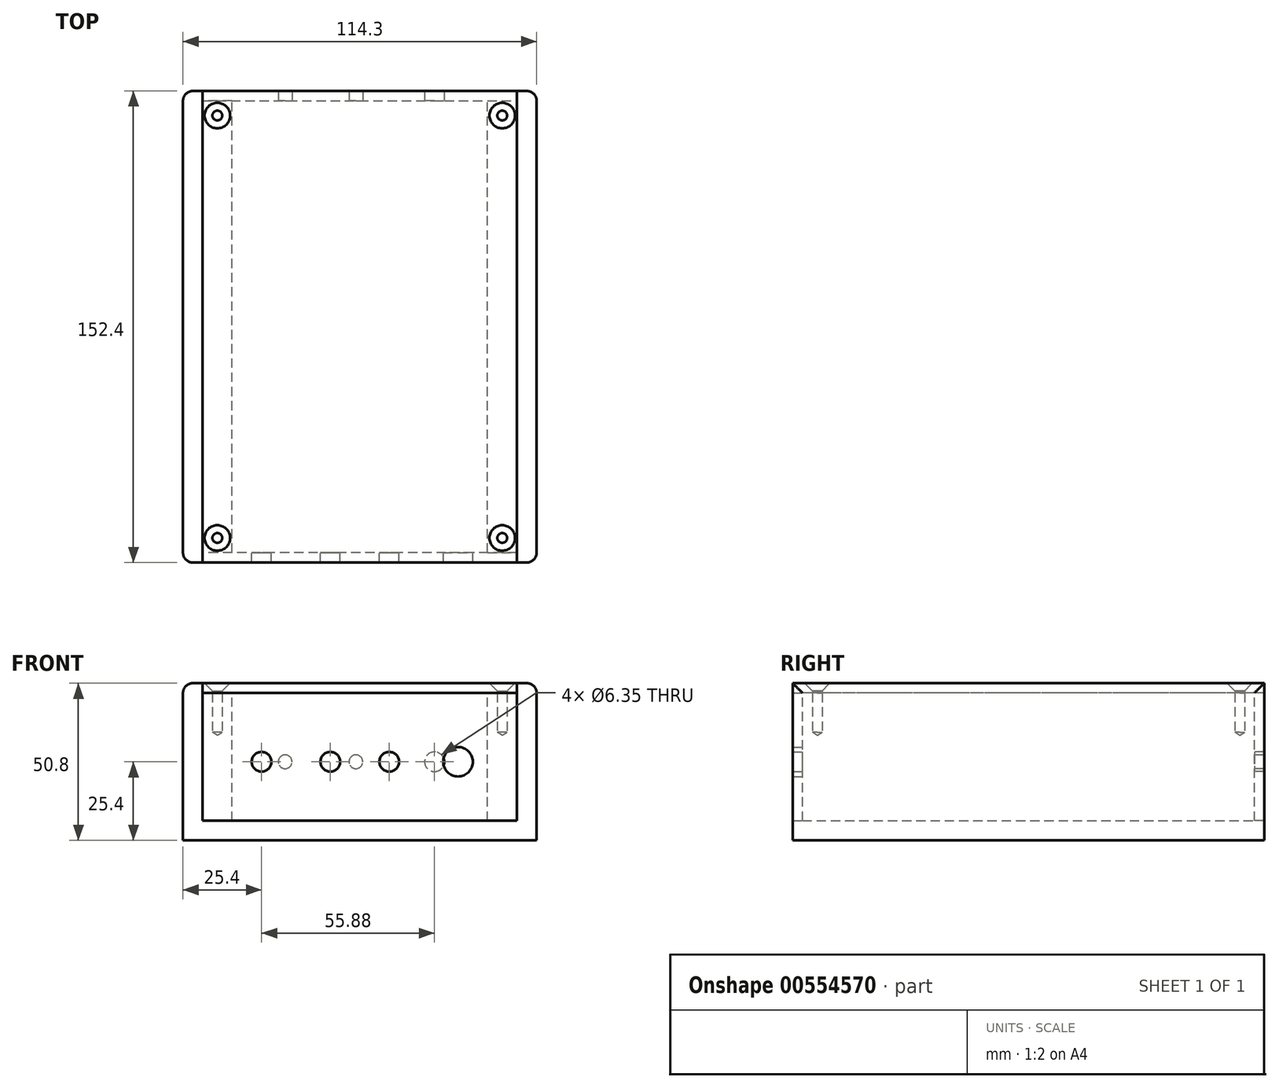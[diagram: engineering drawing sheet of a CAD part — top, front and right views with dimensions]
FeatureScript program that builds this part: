
annotation { "Feature Type Name" : "Feature", "Feature Type Description" : "" }
export const myFeature = defineFeature(function(context is Context, id is Id, definition is map)
    precondition{}
    {
        {
            var Q0;
            Q0=qCreatedBy(makeId("Top.planeOp"),FACE);
            var sketch = newSketch(context, id + "F0", { "sketchPlane" : qUnion([Q0])});
            skLineSegment(sketch, "E0.bottom", {"start": v(57.15, 76.2) * mm, "end": v(-57.15, 76.2) * mm});
            skLineSegment(sketch, "E0.top", {"start": v(57.15, -76.2) * mm, "end": v(-57.15, -76.2) * mm});
            skLineSegment(sketch, "E0.left", {"start": v(57.15, 76.2) * mm, "end": v(57.15, -76.2) * mm});
            skLineSegment(sketch, "E0.right", {"start": v(-57.15, 76.2) * mm, "end": v(-57.15, -76.2) * mm});
            skPoint(sketch, "E0.middle", {"position": v(0, 0) * mm});
            skLineSegment(sketch, "E1", {"start": v(0, -76.2) * mm, "end": v(0, 76.2) * mm, "construction": true});
            skLineSegment(sketch, "E2", {"start": v(-57.15, 0) * mm, "end": v(57.15, 0) * mm, "construction": true});
            skSolve(sketch);
        }
        {
            var Q0;
            Q0=makeQuery(id+"F0.imprint","IMPRINT",FACE,{"disambiguationData":[TD([[makeQuery(id+"F0.imprint","IMPRINT",EDGE,{"derivedFrom":sQuery(id+"F0.wireOp",EDGE,"E0.bottom")}),1.0]])]});
            extrude(context, id + "F1", {"entities" : qUnion([Q0]), "depth" : 50.8 * mm, "offsetDistance" : 25.4 * mm});
        }
        {
            var Q0;
            Q0=makeQuery(id+"F1.opExtrude","CAP_FACE",FACE,{"disambiguationData":[OSD([sQuery(id+"F0.wireOp",EDGE,"E0.bottom"),sQuery(id+"F0.wireOp",EDGE,"E0.top"),sQuery(id+"F0.wireOp",EDGE,"E0.left"),sQuery(id+"F0.wireOp",EDGE,"E0.right")])],"isStart":false});
            var sketch = newSketch(context, id + "F2", { "sketchPlane" : qUnion([Q0])});
            skLineSegment(sketch, "E3.bottom", {"start": v(50.8, 76.2) * mm, "end": v(-50.8, 76.2) * mm});
            skLineSegment(sketch, "E3.top", {"start": v(50.8, -76.2) * mm, "end": v(-50.8, -76.2) * mm});
            skLineSegment(sketch, "E3.left", {"start": v(50.8, 76.2) * mm, "end": v(50.8, -76.2) * mm});
            skLineSegment(sketch, "E3.right", {"start": v(-50.8, 76.2) * mm, "end": v(-50.8, -76.2) * mm});
            skPoint(sketch, "E3.middle", {"position": v(0, 0) * mm});
            skSolve(sketch);
        }
        {
            var Q0;
            Q0 = qSketchRegion(id + "F2", true);
            extrude(context, id + "F3", {"entities" : qUnion([Q0]), "operationType" : NewBodyOperationType.REMOVE, "endBound" : BoundingType.UP_TO_NEXT, "oppositeDirection" : true, "depth" : 25.4 * mm, "hasOffset" : true, "offsetDistance" : 6.35 * mm});
        }
        {
            var Q0;
            Q0=makeQuery(id+"F3.boolean.opBoolean","COPY",FACE,{"derivedFrom":makeQuery(id+"F3.opExtrude","SWEPT_FACE",FACE,{"disambiguationData":[OSD([sQuery(id+"F2.wireOp",EDGE,"E3.left")])]})});
            var sketch = newSketch(context, id + "F4", { "sketchPlane" : qUnion([Q0])});
            skLineSegment(sketch, "E4.bottom", {"start": v(-73.02, 6.35) * mm, "end": v(73.02, 6.35) * mm});
            skLineSegment(sketch, "E4.top", {"start": v(-73.02, 47.63) * mm, "end": v(73.02, 47.63) * mm});
            skLineSegment(sketch, "E4.left", {"start": v(-73.02, 6.35) * mm, "end": v(-73.02, 47.63) * mm});
            skLineSegment(sketch, "E4.right", {"start": v(73.02, 6.35) * mm, "end": v(73.02, 47.63) * mm});
            skPoint(sketch, "E5", {"position": v(0, 6.35) * mm});
            skLineSegment(sketch, "E6", {"start": v(-73.02, 47.63) * mm, "end": v(-73.02, 50.8) * mm, "construction": true});
            skLineSegment(sketch, "E7", {"start": v(-73.02, 47.63) * mm, "end": v(-76.2, 47.63) * mm, "construction": true});
            skSolve(sketch);
        }
        {
            var Q0;
            Q0 = qSketchRegion(id + "F4", true);
            extrude(context, id + "F5", {"entities" : qUnion([Q0]), "operationType" : NewBodyOperationType.ADD, "depth" : 9.52 * mm, "offsetDistance" : 25.4 * mm});
        }
        {
            var Q0;
            Q0=makeQuery(id+"F1.opExtrude","SWEPT_BODY",BODY,{"disambiguationData":[OSD([sQuery(id+"F0.wireOp",EDGE,"E0.bottom"),sQuery(id+"F0.wireOp",EDGE,"E0.top"),sQuery(id+"F0.wireOp",EDGE,"E0.left"),sQuery(id+"F0.wireOp",EDGE,"E0.right")])]});
            var Q1;
            Q1=qCreatedBy(makeId("Right.planeOp"),FACE);
            mirror(context, id + "F6", {"operationType" : NewBodyOperationType.ADD, "entities" : qUnion([Q0]), "mirrorPlane" : qUnion([Q1])});
        }
        {
            var Q0;
            Q0=makeQuery(id+"F1.opExtrude","CAP_EDGE",EDGE,{"disambiguationData":[OSD([sQuery(id+"F0.wireOp",EDGE,"E0.left")])],"isStart":false});
            var Q1;
            Q1=makeQuery(id+"F1.opExtrude","SWEPT_EDGE",EDGE,{"disambiguationData":[OSD([sQuery(id+"F0.wireOp",EDGE,"E0.bottom"),sQuery(id+"F0.wireOp",EDGE,"E0.left")])]});
            var Q2;
            Q2=makeQuery(id+"F1.opExtrude","SWEPT_EDGE",EDGE,{"disambiguationData":[OSD([sQuery(id+"F0.wireOp",EDGE,"E0.top"),sQuery(id+"F0.wireOp",EDGE,"E0.left")])]});
            var Q3;
            Q3=makeQuery(id+"F1.opExtrude","CAP_EDGE",EDGE,{"disambiguationData":[OSD([sQuery(id+"F0.wireOp",EDGE,"E0.right")])],"isStart":false});
            var Q4;
            Q4=makeQuery(id+"F1.opExtrude","SWEPT_EDGE",EDGE,{"disambiguationData":[OSD([sQuery(id+"F0.wireOp",EDGE,"E0.bottom"),sQuery(id+"F0.wireOp",EDGE,"E0.right")])]});
            var Q5;
            Q5=makeQuery(id+"F1.opExtrude","SWEPT_EDGE",EDGE,{"disambiguationData":[OSD([sQuery(id+"F0.wireOp",EDGE,"E0.top"),sQuery(id+"F0.wireOp",EDGE,"E0.right")])]});
            fillet(context, id + "F7", {"entities" : qUnion([Q0, Q1, Q2, Q3, Q4, Q5]), "radius" : 3.17 * mm, "tangentPropagation" : true, "allowEdgeOverflow" : false});
        }
        {
            var Q0;
            Q0=makeQuery(id+"F6.opPattern","COPY",FACE,{"derivedFrom":makeQuery(id+"F5.opExtrude","SWEPT_FACE",FACE,{"disambiguationData":[OSD([sQuery(id+"F4.wireOp",EDGE,"E4.top")])]}),"instanceName":"1"});
            var sketch = newSketch(context, id + "F8", { "sketchPlane" : qUnion([Q0])});
            skLineSegment(sketch, "E8.bottom", {"start": v(50.8, 76.2) * mm, "end": v(-50.8, 76.2) * mm});
            skLineSegment(sketch, "E8.top", {"start": v(50.8, -76.2) * mm, "end": v(-50.8, -76.2) * mm});
            skLineSegment(sketch, "E8.left", {"start": v(50.8, 76.2) * mm, "end": v(50.8, -76.2) * mm});
            skLineSegment(sketch, "E8.right", {"start": v(-50.8, 76.2) * mm, "end": v(-50.8, -76.2) * mm});
            skPoint(sketch, "E8.middle", {"position": v(0, 0) * mm});
            skSolve(sketch);
        }
        {
            var Q0;
            Q0 = qSketchRegion(id + "F8", true);
            var Q1;
            {var subQ0=sQuery(id+"F0.wireOp",EDGE,"E0.bottom");var subQ1=sQuery(id+"F0.wireOp",EDGE,"E0.right");var subQ2=sQuery(id+"F0.wireOp",EDGE,"E0.top");Q1=makeQuery(id+"F3.boolean.opBoolean","SPLIT",FACE,{"disambiguationData":[TD([makeQuery(id+"F1.opExtrude","SWEPT_FACE",FACE,{"disambiguationData":[OSD([subQ1])]})])],"derivedFrom":makeQuery(id+"F1.opExtrude","CAP_FACE",FACE,{"disambiguationData":[OSD([subQ0,subQ2,sQuery(id+"F0.wireOp",EDGE,"E0.left"),subQ1])],"isStart":false})});}
            extrude(context, id + "F9", {"entities" : qUnion([Q0]), "endBound" : BoundingType.UP_TO_SURFACE, "depth" : 25.4 * mm, "endBoundEntityFace" : qUnion([Q1]), "offsetDistance" : 25.4 * mm});
        }
        {
            var Q0;
            {var subQ0=sQuery(id+"F0.wireOp",EDGE,"E0.bottom");var subQ1=sQuery(id+"F0.wireOp",EDGE,"E0.right");var subQ2=sQuery(id+"F0.wireOp",EDGE,"E0.top");Q0=makeQuery(id+"F3.boolean.opBoolean","SPLIT",FACE,{"disambiguationData":[TD([makeQuery(id+"F1.opExtrude","SWEPT_FACE",FACE,{"disambiguationData":[OSD([subQ1])]})])],"derivedFrom":makeQuery(id+"F1.opExtrude","CAP_FACE",FACE,{"disambiguationData":[OSD([subQ0,subQ2,sQuery(id+"F0.wireOp",EDGE,"E0.left"),subQ1])],"isStart":false})});}
            var sketch = newSketch(context, id + "F10", { "sketchPlane" : qUnion([Q0])});
            skLineSegment(sketch, "E9.bottom", {"start": v(-46.04, 68.26) * mm, "end": v(46.04, 68.26) * mm, "construction": true});
            skLineSegment(sketch, "E9.top", {"start": v(-46.04, -68.26) * mm, "end": v(46.04, -68.26) * mm, "construction": true});
            skLineSegment(sketch, "E9.left", {"start": v(-46.04, 68.26) * mm, "end": v(-46.04, -68.26) * mm, "construction": true});
            skLineSegment(sketch, "E9.right", {"start": v(46.04, 68.26) * mm, "end": v(46.04, -68.26) * mm, "construction": true});
            skPoint(sketch, "E9.middle", {"position": v(0, 0) * mm});
            skLineSegment(sketch, "E10", {"start": v(-46.04, 68.26) * mm, "end": v(-46.04, 73.02) * mm, "construction": true});
            skLineSegment(sketch, "E11", {"start": v(-46.04, 68.26) * mm, "end": v(-50.8, 68.26) * mm, "construction": true});
            skSolve(sketch);
        }
        {
            var Q0;
            Q0=sQuery(id+"F10.wireOp",VERTEX,"E9.left.end");
            var Q1;
            Q1=sQuery(id+"F10.wireOp",VERTEX,"E9.right.end");
            var Q2;
            Q2=sQuery(id+"F10.wireOp",VERTEX,"E9.right.start");
            var Q3;
            Q3=sQuery(id+"F10.wireOp",VERTEX,"E9.bottom.start");
            var Q4;
            Q4=makeQuery(id+"F1.opExtrude","SWEPT_BODY",BODY,{"disambiguationData":[OSD([sQuery(id+"F0.wireOp",EDGE,"E0.bottom"),sQuery(id+"F0.wireOp",EDGE,"E0.top"),sQuery(id+"F0.wireOp",EDGE,"E0.left"),sQuery(id+"F0.wireOp",EDGE,"E0.right")])]});
            var Q5;
            Q5=makeQuery(id+"F9.opExtrude","SWEPT_BODY",BODY,{"disambiguationData":[OSD([sQuery(id+"F8.wireOp",EDGE,"E8.bottom"),sQuery(id+"F8.wireOp",EDGE,"E8.top"),sQuery(id+"F8.wireOp",EDGE,"E8.left"),sQuery(id+"F8.wireOp",EDGE,"E8.right")])]});
            hole(context, id + "F11", {"style" : HoleStyle.C_SINK, "endStyle" : HoleEndStyle.BLIND, "holeDiameter" : 3.17 * mm, "cSinkDiameter" : 8.25 * mm, "cSinkAngle" : 90 * degree, "holeDepth" : 15.88 * mm, "isTappedThrough" : true, "tappedDepth" : 12.7 * mm, "tapClearance" : 3, "locations" : qUnion([Q0, Q1, Q2, Q3]), "scope" : qUnion([Q4, Q5])});
        }
        {
            var Q0;
            Q0=makeQuery(id+"F6.opPattern","COPY",FACE,{"derivedFrom":makeQuery(id+"F5.opExtrude","SWEPT_FACE",FACE,{"disambiguationData":[OSD([sQuery(id+"F4.wireOp",EDGE,"E4.right")])]}),"instanceName":"1"});
            var sketch = newSketch(context, id + "F12", { "sketchPlane" : qUnion([Q0])});
            skLineSegment(sketch, "E12.bottom", {"start": v(-50.8, 47.63) * mm, "end": v(50.8, 47.63) * mm});
            skLineSegment(sketch, "E12.top", {"start": v(-50.8, 6.35) * mm, "end": v(50.8, 6.35) * mm});
            skLineSegment(sketch, "E12.left", {"start": v(-50.8, 47.63) * mm, "end": v(-50.8, 6.35) * mm});
            skLineSegment(sketch, "E12.right", {"start": v(50.8, 47.63) * mm, "end": v(50.8, 6.35) * mm});
            skLineSegment(sketch, "E13", {"start": v(0, 0) * mm, "end": v(0, 50.8) * mm, "construction": true});
            skCircle(sketch, "E14", {"center": v(-31.75, 25.4) * mm, "radius": 3.18 * mm});
            skPoint(sketch, "E14.centerSnap0", {"position": v(0, 25.4) * mm});
            skCircle(sketch, "E15", {"center": v(-31.75, 25.4) * mm, "radius": 9.53 * mm, "construction": true});
            skCircle(sketch, "E16", {"center": v(-9.52, 25.4) * mm, "radius": 3.18 * mm});
            skLineSegment(sketch, "E17.bottom", {"start": v(-3.17, 31.75) * mm, "end": v(-15.88, 31.75) * mm, "construction": true});
            skLineSegment(sketch, "E17.top", {"start": v(-3.18, 19.05) * mm, "end": v(-15.88, 19.05) * mm, "construction": true});
            skLineSegment(sketch, "E17.left", {"start": v(-3.17, 31.75) * mm, "end": v(-3.18, 19.05) * mm, "construction": true});
            skLineSegment(sketch, "E17.right", {"start": v(-15.88, 31.75) * mm, "end": v(-15.88, 19.05) * mm, "construction": true});
            skCircle(sketch, "E18", {"center": v(9.53, 25.4) * mm, "radius": 3.18 * mm});
            skLineSegment(sketch, "E19.bottom", {"start": v(15.88, 31.75) * mm, "end": v(3.18, 31.75) * mm, "construction": true});
            skLineSegment(sketch, "E19.top", {"start": v(15.88, 19.05) * mm, "end": v(3.18, 19.05) * mm, "construction": true});
            skLineSegment(sketch, "E19.left", {"start": v(15.88, 31.75) * mm, "end": v(15.88, 19.05) * mm, "construction": true});
            skLineSegment(sketch, "E19.right", {"start": v(3.18, 31.75) * mm, "end": v(3.18, 19.05) * mm, "construction": true});
            skLineSegment(sketch, "E20", {"start": v(-9.52, 25.4) * mm, "end": v(9.53, 25.4) * mm, "construction": true});
            skCircle(sketch, "E21", {"center": v(31.75, 25.4) * mm, "radius": 4.76 * mm});
            skCircle(sketch, "E22", {"center": v(31.75, 25.4) * mm, "radius": 8.26 * mm, "construction": true});
            skSolve(sketch);
        }
        {
            var Q0;
            Q0 = qSketchRegion(id + "F12", true);
            var Q1;
            Q1=makeQuery(id+"F1.opExtrude","SWEPT_FACE",FACE,{"disambiguationData":[OSD([sQuery(id+"F0.wireOp",EDGE,"E0.top")])]});
            extrude(context, id + "F13", {"entities" : qUnion([Q0]), "endBound" : BoundingType.UP_TO_SURFACE, "depth" : 25.4 * mm, "endBoundEntityFace" : qUnion([Q1]), "offsetDistance" : 25.4 * mm});
        }
        {
            var Q0;
            Q0=makeQuery(id+"F5.opExtrude","SWEPT_FACE",FACE,{"disambiguationData":[OSD([sQuery(id+"F4.wireOp",EDGE,"E4.left")])]});
            var sketch = newSketch(context, id + "F14", { "sketchPlane" : qUnion([Q0])});
            skLineSegment(sketch, "E23.bottom", {"start": v(-50.8, 47.63) * mm, "end": v(50.8, 47.63) * mm});
            skLineSegment(sketch, "E23.top", {"start": v(-50.8, 6.35) * mm, "end": v(50.8, 6.35) * mm});
            skLineSegment(sketch, "E23.left", {"start": v(-50.8, 47.63) * mm, "end": v(-50.8, 6.35) * mm});
            skLineSegment(sketch, "E23.right", {"start": v(50.8, 47.63) * mm, "end": v(50.8, 6.35) * mm});
            skLineSegment(sketch, "E24", {"start": v(0, 0) * mm, "end": v(0, 50.8) * mm, "construction": true});
            skCircle(sketch, "E25", {"center": v(-24.13, 25.4) * mm, "radius": 3.18 * mm});
            skPoint(sketch, "E25.centerSnap0", {"position": v(0, 25.4) * mm});
            skCircle(sketch, "E26", {"center": v(1.27, 25.4) * mm, "radius": 2.22 * mm});
            skCircle(sketch, "E27", {"center": v(24.13, 25.4) * mm, "radius": 2.22 * mm});
            skLineSegment(sketch, "E28", {"start": v(-24.13, 25.4) * mm, "end": v(24.13, 25.4) * mm, "construction": true});
            skSolve(sketch);
        }
        {
            var Q0;
            Q0 = qSketchRegion(id + "F14", true);
            var Q1;
            Q1=makeQuery(id+"F1.opExtrude","SWEPT_FACE",FACE,{"disambiguationData":[OSD([sQuery(id+"F0.wireOp",EDGE,"E0.bottom")])]});
            extrude(context, id + "F15", {"entities" : qUnion([Q0]), "endBound" : BoundingType.UP_TO_SURFACE, "depth" : 25.4 * mm, "endBoundEntityFace" : qUnion([Q1]), "offsetDistance" : 25.4 * mm});
        }
    });
